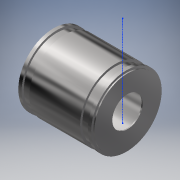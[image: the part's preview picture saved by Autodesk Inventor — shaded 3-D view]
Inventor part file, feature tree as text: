
AUTODESK INVENTOR PART (.ipt)
format: ipt  version: 2018 (Build 220112000, 112)  size: 183,808 bytes
history: native  units: in
note: dims shown in document units (in); Inventor stores cm internally (conversion verified against a paired STEP export)
features: reference x7, other x5, revolve x1, sketch x1
ambient origin geometry x8: Origin, YZ Plane, XZ Plane, XY Plane, X Axis, Y Axis, Z Axis, Center Point
bodies: Solid1 (feature_tree)
feature tree (14):
  revolve  "Revolution1"  [1 undecoded]
  sketch  "Sketch1"  dims[d0=36.0in d3=6.0in d4=4.0in d5=4.0in d6=4.0in d7=90.0deg d12=132.066in d14=4.0in]
  reference  "Reference1"
  reference  "Reference2"
  reference  "Reference3"
  reference  "Reference4"
  reference  "Reference5"
  reference  "Reference6"
  reference  "Reference7"
  other  "FinalFerrisWheelWeek3.5Drivable.iam"
  other  "InsideMiddleShaftCJE:1"
  other  "FullWheelWeek3AJB:1"
  other  "InnerRingAJB:2"
  other  "InnerRingAJB:1"
note: 1 required parameter value undecoded (feature->parameter linkage not recoverable at this tier; creation-order binding heuristic only, values carry confidence <= 0.55)
